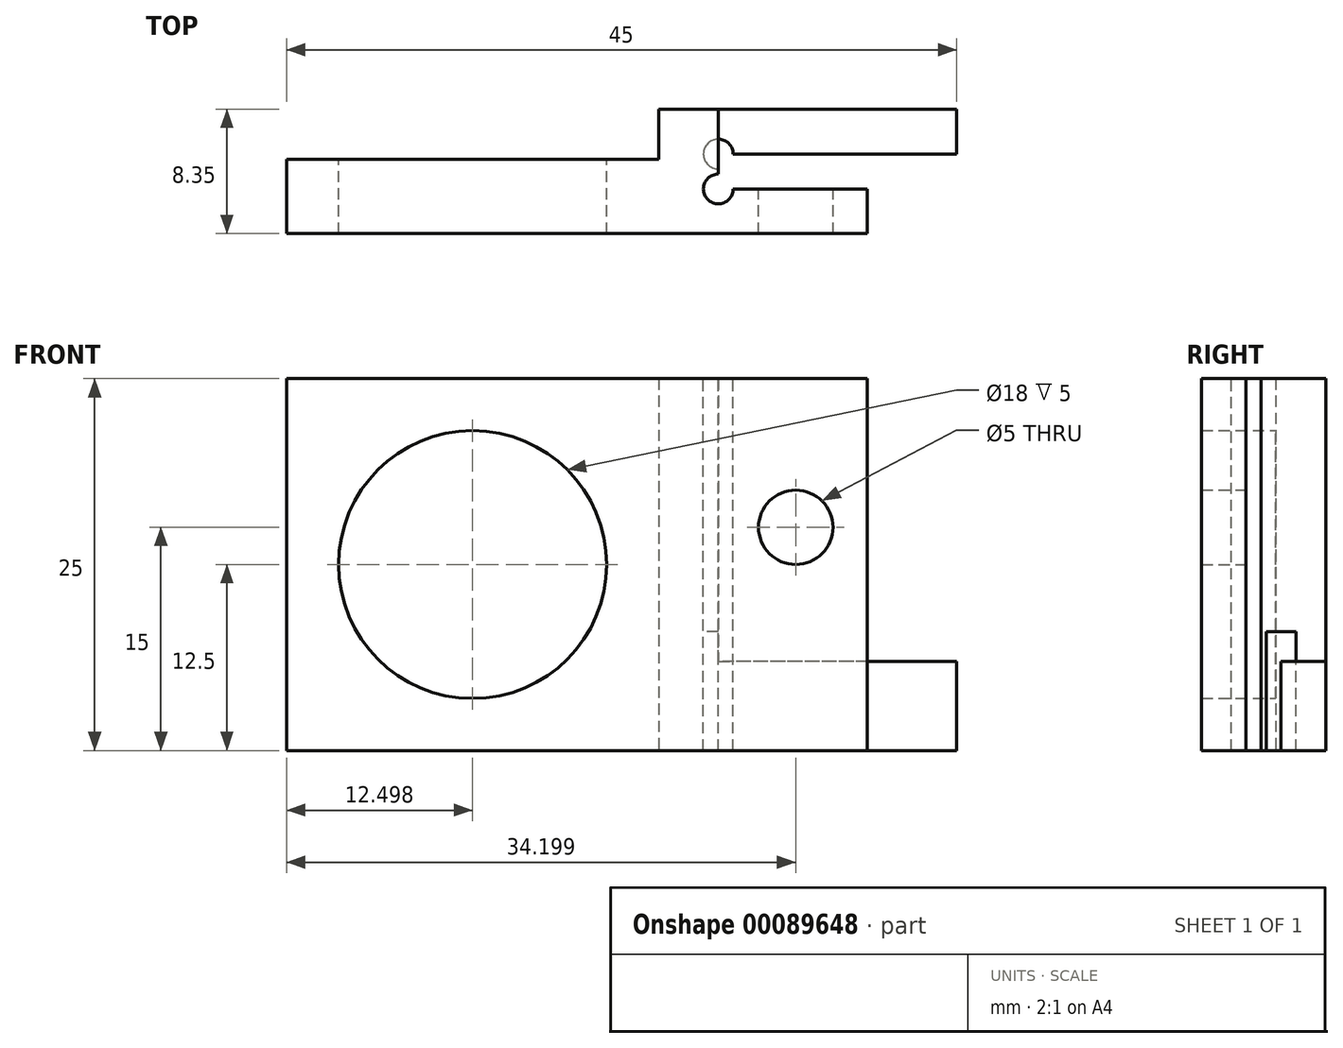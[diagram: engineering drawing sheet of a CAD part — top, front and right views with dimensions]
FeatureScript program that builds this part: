
annotation { "Feature Type Name" : "Feature", "Feature Type Description" : "" }
export const myFeature = defineFeature(function(context is Context, id is Id, definition is map)
    precondition{}
    {
        {
            var Q0;
            Q0=qCreatedBy(makeId("Top.planeOp"),FACE);
            var sketch = newSketch(context, id + "F0", { "sketchPlane" : qUnion([Q0])});
            skLineSegment(sketch, "E0", {"start": v(1.7, 2.79) * mm, "end": v(11.7, 2.79) * mm});
            skLineSegment(sketch, "E1", {"start": v(11.7, 2.79) * mm, "end": v(11.7, 5.79) * mm});
            skLineSegment(sketch, "E2", {"start": v(11.7, 5.79) * mm, "end": v(-2.3, 5.79) * mm});
            skLineSegment(sketch, "E3", {"start": v(-2.3, 5.79) * mm, "end": v(-2.3, 2.44) * mm});
            skLineSegment(sketch, "E4", {"start": v(-2.3, 2.44) * mm, "end": v(-27.3, 2.44) * mm});
            skLineSegment(sketch, "E5", {"start": v(-27.3, 2.44) * mm, "end": v(-27.3, -2.56) * mm});
            skLineSegment(sketch, "E6", {"start": v(11.7, -2.56) * mm, "end": v(11.7, 0.44) * mm});
            skLineSegment(sketch, "E7", {"start": v(11.7, 0.44) * mm, "end": v(1.7, 0.44) * mm});
            skLineSegment(sketch, "E8", {"start": v(1.7, 0.44) * mm, "end": v(1.7, 2.79) * mm});
            skLineSegment(sketch, "E9", {"start": v(11.7, -2.56) * mm, "end": v(-27.3, -2.56) * mm});
            skSolve(sketch);
        }
        {
            var Q0;
            Q0=makeQuery(id+"F0.imprint","IMPRINT",FACE,{"disambiguationData":[TD([[makeQuery(id+"F0.imprint","IMPRINT",EDGE,{"derivedFrom":sQuery(id+"F0.wireOp",EDGE,"E0")}),1.0]])]});
            extrude(context, id + "F1", {"entities" : qUnion([Q0]), "depth" : 25 * mm});
        }
        {
            var Q0;
            Q0=makeQuery(id+"F1.opExtrude","SWEPT_FACE",FACE,{"disambiguationData":[OSD([sQuery(id+"F0.wireOp",EDGE,"E2")])]});
            var sketch = newSketch(context, id + "F2", { "sketchPlane" : qUnion([Q0])});
            skLineSegment(sketch, "E10.bottom", {"start": v(-11.7, 25) * mm, "end": v(-1.7, 25) * mm});
            skLineSegment(sketch, "E10.top", {"start": v(-11.7, 6) * mm, "end": v(-1.7, 6) * mm});
            skLineSegment(sketch, "E10.left", {"start": v(-11.7, 25) * mm, "end": v(-11.7, 6) * mm});
            skLineSegment(sketch, "E10.right", {"start": v(-1.7, 25) * mm, "end": v(-1.7, 6) * mm});
            skSolve(sketch);
        }
        {
            var Q0;
            Q0=makeQuery(id+"F2.imprint","IMPRINT",FACE,{"disambiguationData":[TD([[makeQuery(id+"F2.imprint","IMPRINT",EDGE,{"derivedFrom":sQuery(id+"F2.wireOp",EDGE,"E10.bottom")}),-1.0]])]});
            extrude(context, id + "F3", {"entities" : qUnion([Q0]), "operationType" : NewBodyOperationType.REMOVE, "oppositeDirection" : true, "depth" : 3 * mm});
        }
        {
            var Q0;
            Q0=makeQuery(id+"F1.opExtrude","SWEPT_FACE",FACE,{"disambiguationData":[OSD([sQuery(id+"F0.wireOp",EDGE,"E4")])]});
            var sketch = newSketch(context, id + "F4", { "sketchPlane" : qUnion([Q0])});
            skCircle(sketch, "E11", {"center": v(14.8, 12.5) * mm, "radius": 9 * mm});
            skPoint(sketch, "E12", {"position": v(27.3, 12.5) * mm});
            skPoint(sketch, "E13", {"position": v(14.8, 0) * mm});
            skSolve(sketch);
        }
        {
            var Q0;
            Q0=makeQuery(id+"F4.imprint","IMPRINT",FACE,{"disambiguationData":[TD([[makeQuery(id+"F4.imprint","IMPRINT",EDGE,{"derivedFrom":sQuery(id+"F4.wireOp",EDGE,"E11")}),1.0]])]});
            extrude(context, id + "F5", {"entities" : qUnion([Q0]), "operationType" : NewBodyOperationType.REMOVE, "oppositeDirection" : true, "depth" : 10 * mm});
        }
        {
            var Q0;
            Q0=makeQuery(id+"F1.opExtrude","SWEPT_FACE",FACE,{"disambiguationData":[OSD([sQuery(id+"F0.wireOp",EDGE,"E7")])]});
            var sketch = newSketch(context, id + "F6", { "sketchPlane" : qUnion([Q0])});
            skCircle(sketch, "E14", {"center": v(-6.9, 15) * mm, "radius": 2.5 * mm});
            skSolve(sketch);
        }
        {
            var Q0;
            Q0=makeQuery(id+"F6.imprint","IMPRINT",FACE,{"disambiguationData":[TD([[makeQuery(id+"F6.imprint","IMPRINT",EDGE,{"derivedFrom":sQuery(id+"F6.wireOp",EDGE,"E14")}),1.0]])]});
            extrude(context, id + "F7", {"entities" : qUnion([Q0]), "operationType" : NewBodyOperationType.REMOVE, "oppositeDirection" : true, "depth" : 25 * mm});
        }
        {
            var Q0;
            Q0=makeQuery(id+"F1.opExtrude","SWEPT_FACE",FACE,{"disambiguationData":[OSD([sQuery(id+"F0.wireOp",EDGE,"E1")])]});
            var sketch = newSketch(context, id + "F8", { "sketchPlane" : qUnion([Q0])});
            skLineSegment(sketch, "E15.bottom", {"start": v(2.79, 0) * mm, "end": v(5.79, 0) * mm});
            skLineSegment(sketch, "E15.top", {"start": v(2.79, 6) * mm, "end": v(5.79, 6) * mm});
            skLineSegment(sketch, "E15.left", {"start": v(2.79, 0) * mm, "end": v(2.79, 6) * mm});
            skLineSegment(sketch, "E15.right", {"start": v(5.79, 0) * mm, "end": v(5.79, 6) * mm});
            skSolve(sketch);
        }
        {
            var Q0;
            Q0 = qSketchRegion(id + "F8", true);
            extrude(context, id + "F9", {"entities" : qUnion([Q0]), "operationType" : NewBodyOperationType.ADD, "depth" : 6 * mm});
        }
        {
            var Q0;
            Q0=makeQuery(id+"F1.opExtrude","CAP_FACE",FACE,{"disambiguationData":[OSD([sQuery(id+"F0.wireOp",EDGE,"E0"),sQuery(id+"F0.wireOp",EDGE,"E1"),sQuery(id+"F0.wireOp",EDGE,"E2"),sQuery(id+"F0.wireOp",EDGE,"E3"),sQuery(id+"F0.wireOp",EDGE,"E4"),sQuery(id+"F0.wireOp",EDGE,"E5"),sQuery(id+"F0.wireOp",EDGE,"E6"),sQuery(id+"F0.wireOp",EDGE,"E7"),sQuery(id+"F0.wireOp",EDGE,"E8"),sQuery(id+"F0.wireOp",EDGE,"E9")])],"isStart":false});
            var sketch = newSketch(context, id + "F10", { "sketchPlane" : qUnion([Q0])});
            skCircle(sketch, "E16", {"center": v(1.7, 0.44) * mm, "radius": 1 * mm});
            skSolve(sketch);
        }
        {
            var Q0;
            Q0 = qSketchRegion(id + "F10", true);
            extrude(context, id + "F11", {"entities" : qUnion([Q0]), "operationType" : NewBodyOperationType.REMOVE, "oppositeDirection" : true, "depth" : 25 * mm});
        }
        {
            var Q0;
            Q0=makeQuery(id+"F9.boolean.opBoolean","MERGE",FACE,{"derivedFrom":[makeQuery(id+"F3.boolean.opBoolean","COPY",FACE,{"derivedFrom":makeQuery(id+"F3.opExtrude","SWEPT_FACE",FACE,{"disambiguationData":[OSD([sQuery(id+"F2.wireOp",EDGE,"E10.top")])]})}),makeQuery(id+"F9.opExtrude","SWEPT_FACE",FACE,{"disambiguationData":[OSD([sQuery(id+"F8.wireOp",EDGE,"E15.top")])]})]});
            var sketch = newSketch(context, id + "F12", { "sketchPlane" : qUnion([Q0])});
            skCircle(sketch, "E17", {"center": v(1.7, 2.79) * mm, "radius": 1 * mm});
            skSolve(sketch);
        }
        {
            var Q0;
            {var subQ0=sQuery(id+"F12.wireOp",EDGE,"E17");var subQ1=sQuery(id+"F2.wireOp",EDGE,"E10.top");var subQ2=makeQuery(id+"F3.boolean.opBoolean","COPY",EDGE,{"derivedFrom":makeQuery(id+"F3.opExtrude","SWEPT_EDGE",EDGE,{"disambiguationData":[OSD([subQ1,sQuery(id+"F2.wireOp",EDGE,"E10.right")])]})});var subQ3=makeQuery(id+"F12.imprint","INTERSECT",VERTEX,{"derivedFrom":[subQ2,subQ0]});Q0=makeQuery(id+"F12.imprint","IMPRINT",FACE,{"disambiguationData":[TD([[makeQuery(id+"F12.imprint","IMPRINT",EDGE,{"disambiguationData":[TD([[subQ3,-1.0]])],"derivedFrom":subQ0}),1.0]])]});}
            var Q1;
            {var subQ0=sQuery(id+"F12.wireOp",EDGE,"E17");var subQ1=sQuery(id+"F2.wireOp",EDGE,"E10.top");var subQ2=makeQuery(id+"F3.boolean.opBoolean","COPY",EDGE,{"derivedFrom":makeQuery(id+"F3.opExtrude","SWEPT_EDGE",EDGE,{"disambiguationData":[OSD([subQ1,sQuery(id+"F2.wireOp",EDGE,"E10.right")])]})});var subQ3=makeQuery(id+"F12.imprint","INTERSECT",VERTEX,{"derivedFrom":[subQ2,subQ0]});Q1=makeQuery(id+"F12.imprint","IMPRINT",FACE,{"disambiguationData":[TD([[makeQuery(id+"F12.imprint","IMPRINT",EDGE,{"disambiguationData":[TD([[subQ3,1.0]])],"derivedFrom":subQ0}),1.0]])]});}
            extrude(context, id + "F13", {"entities" : qUnion([Q0, Q1]), "operationType" : NewBodyOperationType.REMOVE, "oppositeDirection" : true, "depth" : 25 * mm, "hasSecondDirection" : true, "secondDirectionOppositeDirection" : false, "secondDirectionDepth" : 2 * mm});
        }
    });
